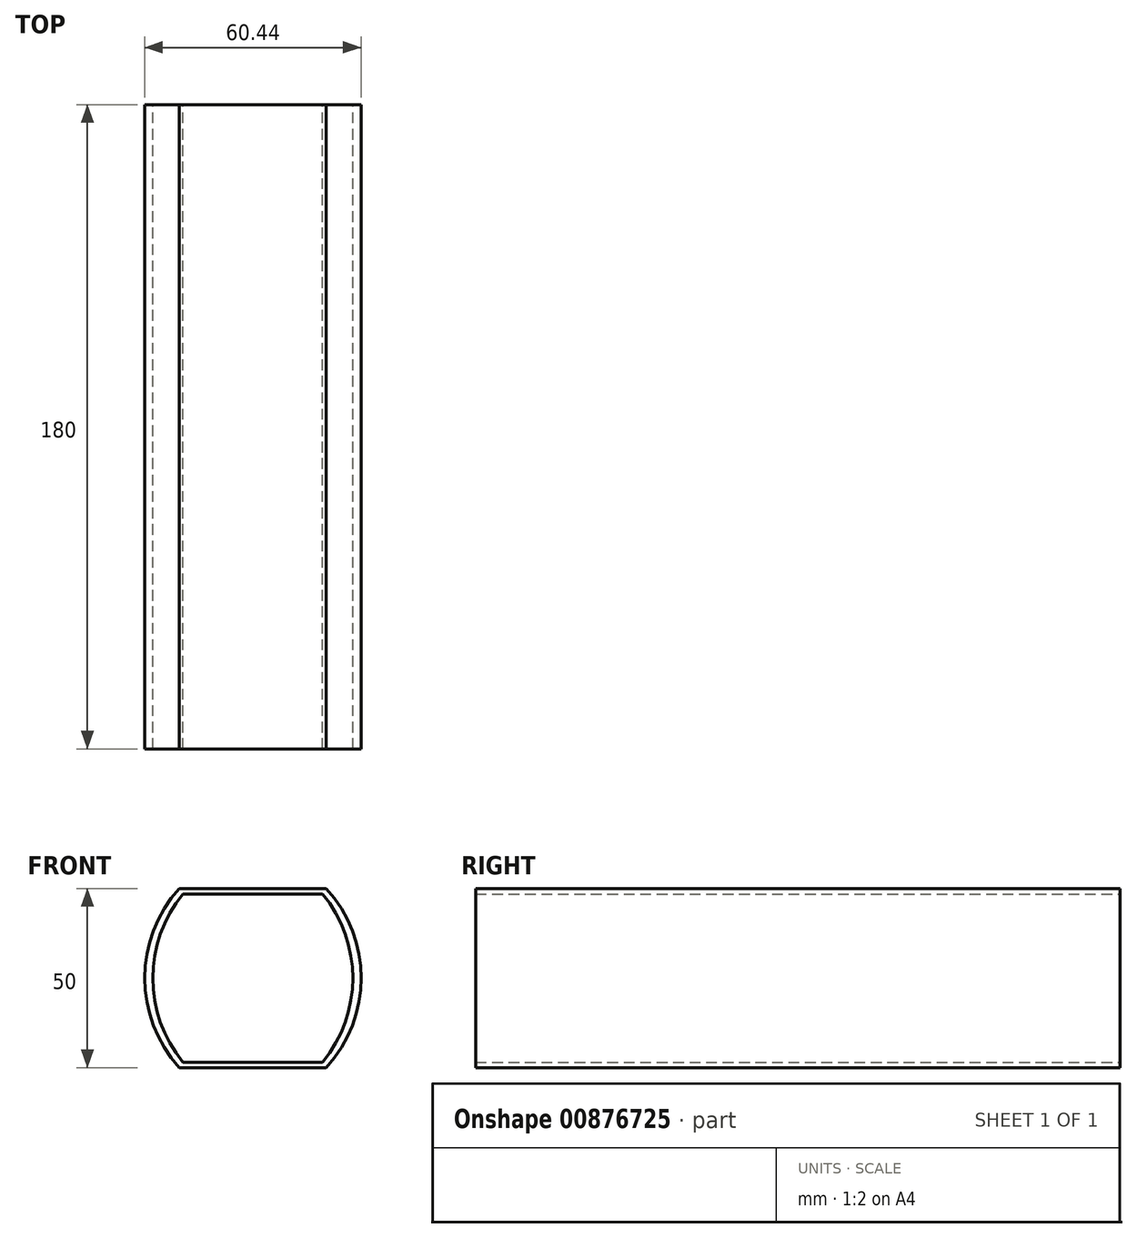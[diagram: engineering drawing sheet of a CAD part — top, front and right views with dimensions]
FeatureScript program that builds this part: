
annotation { "Feature Type Name" : "Feature", "Feature Type Description" : "" }
export const myFeature = defineFeature(function(context is Context, id is Id, definition is map)
    precondition{}
    {
        {
            var Q0;
            Q0=qCreatedBy(makeId("Front.planeOp"),FACE);
            var sketch = newSketch(context, id + "F0", { "sketchPlane" : qUnion([Q0])});
            skLineSegment(sketch, "E0.bottom", {"start": v(19.5, -23.5) * mm, "end": v(-19.5, -23.5) * mm});
            skLineSegment(sketch, "E0.top", {"start": v(19.5, 23.5) * mm, "end": v(-19.5, 23.5) * mm});
            skPoint(sketch, "E0.middle", {"position": v(0, 0) * mm});
            skArc(sketch, "E1", {"start": v(-19.5, 23.5) * mm, "mid": v(-27.92, 0) * mm, "end": v(-19.5, -23.5) * mm});
            skArc(sketch, "E2", {"start": v(19.5, -23.5) * mm, "mid": v(27.92, 0) * mm, "end": v(19.5, 23.5) * mm});
            skLineSegment(sketch, "E3.bottom", {"start": v(20.5, -25) * mm, "end": v(-20.5, -25) * mm});
            skLineSegment(sketch, "E3.top", {"start": v(20.5, 25) * mm, "end": v(-20.5, 25) * mm});
            skArc(sketch, "E4", {"start": v(-20.5, 25) * mm, "mid": v(-30.22, 0) * mm, "end": v(-20.5, -25) * mm});
            skArc(sketch, "E5", {"start": v(20.5, -25) * mm, "mid": v(30.22, 0) * mm, "end": v(20.5, 25) * mm});
            skSolve(sketch);
        }
        {
            var Q0;
            Q0=makeQuery(id+"F0.imprint","IMPRINT",FACE,{"disambiguationData":[TD([[makeQuery(id+"F0.imprint","IMPRINT",EDGE,{"derivedFrom":sQuery(id+"F0.wireOp",EDGE,"E0.bottom")}),1.0]])]});
            extrude(context, id + "F1", {"entities" : qUnion([Q0]), "depth" : 180 * mm, "offsetDistance" : 25 * mm});
        }
    });
